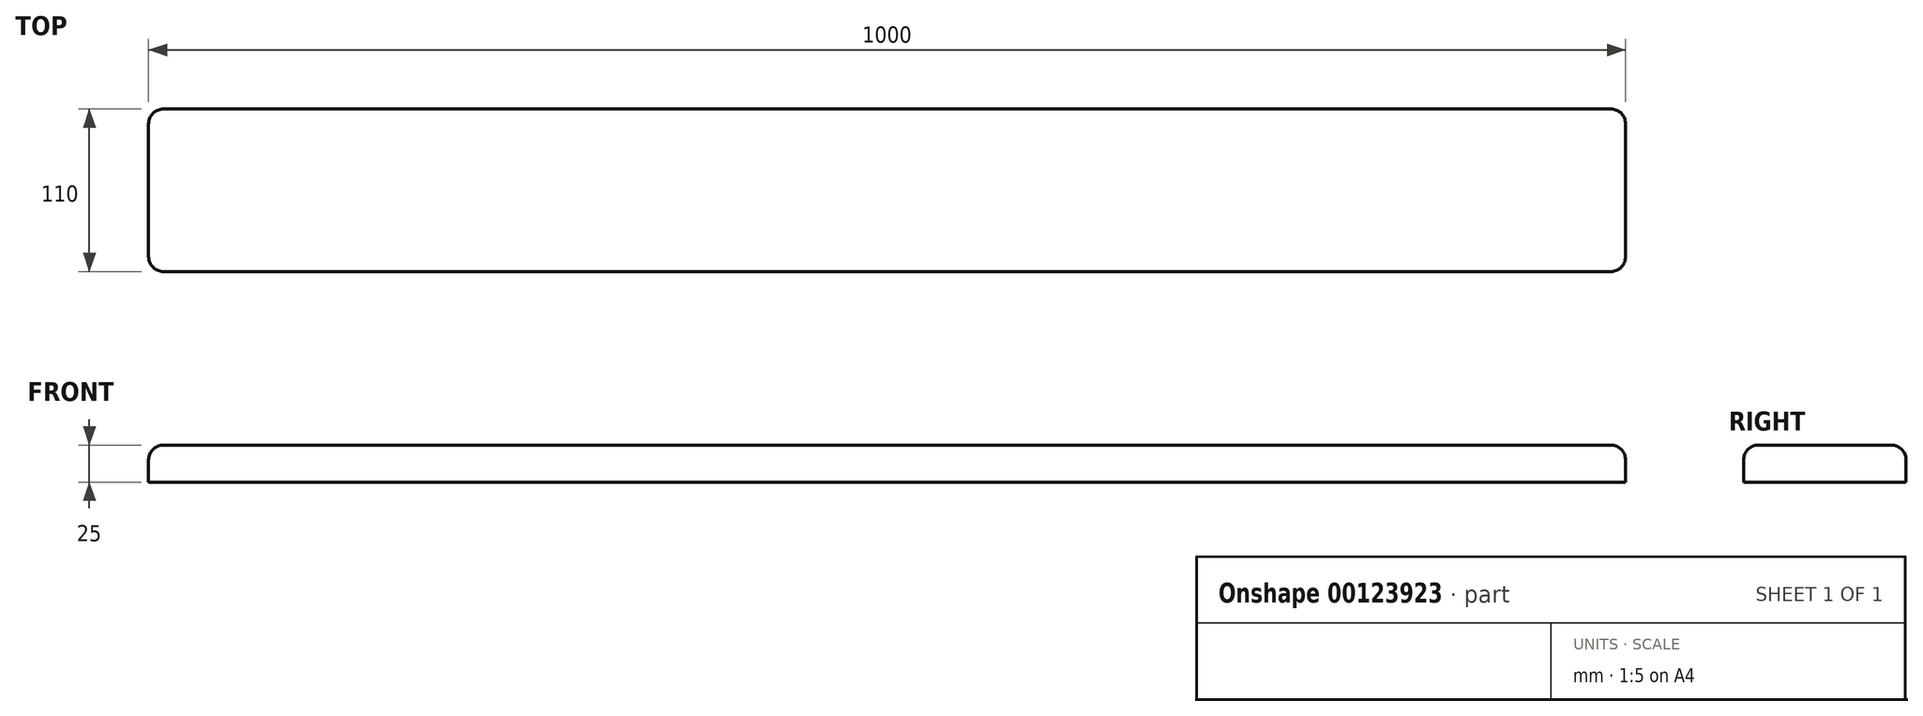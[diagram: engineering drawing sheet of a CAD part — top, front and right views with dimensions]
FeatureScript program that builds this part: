
annotation { "Feature Type Name" : "Feature", "Feature Type Description" : "" }
export const myFeature = defineFeature(function(context is Context, id is Id, definition is map)
    precondition{}
    {
        {
            var Q0;
            Q0=qCreatedBy(makeId("Right.planeOp"),FACE);
            var sketch = newSketch(context, id + "F0", { "sketchPlane" : qUnion([Q0])});
            skLineSegment(sketch, "E0.bottom", {"start": v(55, -12.5) * mm, "end": v(-55, -12.5) * mm});
            skLineSegment(sketch, "E0.top", {"start": v(45, 12.5) * mm, "end": v(-45, 12.5) * mm});
            skLineSegment(sketch, "E0.left", {"start": v(55, -12.5) * mm, "end": v(55, 2.5) * mm});
            skLineSegment(sketch, "E0.right", {"start": v(-55, -12.5) * mm, "end": v(-55, 2.5) * mm});
            skPoint(sketch, "E0.middle", {"position": v(0, 0) * mm});
            skPoint(sketch, "E1.visualSharp", {"position": v(-55, 12.5) * mm});
            skArc(sketch, "E1.filletArc", {"start": v(-45, 12.5) * mm, "mid": v(-52.07, 9.57) * mm, "end": v(-55, 2.5) * mm});
            skPoint(sketch, "E2.visualSharp", {"position": v(55, 12.5) * mm});
            skArc(sketch, "E2.filletArc", {"start": v(55, 2.5) * mm, "mid": v(52.07, 9.57) * mm, "end": v(45, 12.5) * mm});
            skSolve(sketch);
        }
        {
            var Q0;
            Q0=makeQuery(id+"F0.imprint","IMPRINT",FACE,{"disambiguationData":[TD([[makeQuery(id+"F0.imprint","IMPRINT",EDGE,{"derivedFrom":sQuery(id+"F0.wireOp",EDGE,"E0.bottom")}),-1.0]])]});
            extrude(context, id + "F1", {"entities" : qUnion([Q0]), "depth" : 1000 * mm});
        }
        {
            var Q0;
            Q0=makeQuery(id+"F1.opExtrude","CAP_EDGE",EDGE,{"disambiguationData":[OSD([sQuery(id+"F0.wireOp",EDGE,"E0.top")])],"isStart":false});
            var Q1;
            Q1=makeQuery(id+"F1.opExtrude","SWEPT_FACE",FACE,{"disambiguationData":[OSD([sQuery(id+"F0.wireOp",EDGE,"E0.top")])]});
            fillet(context, id + "F2", {"entities" : qUnion([Q0, Q1]), "radius" : 10 * mm, "tangentPropagation" : true, "allowEdgeOverflow" : false});
        }
    });
